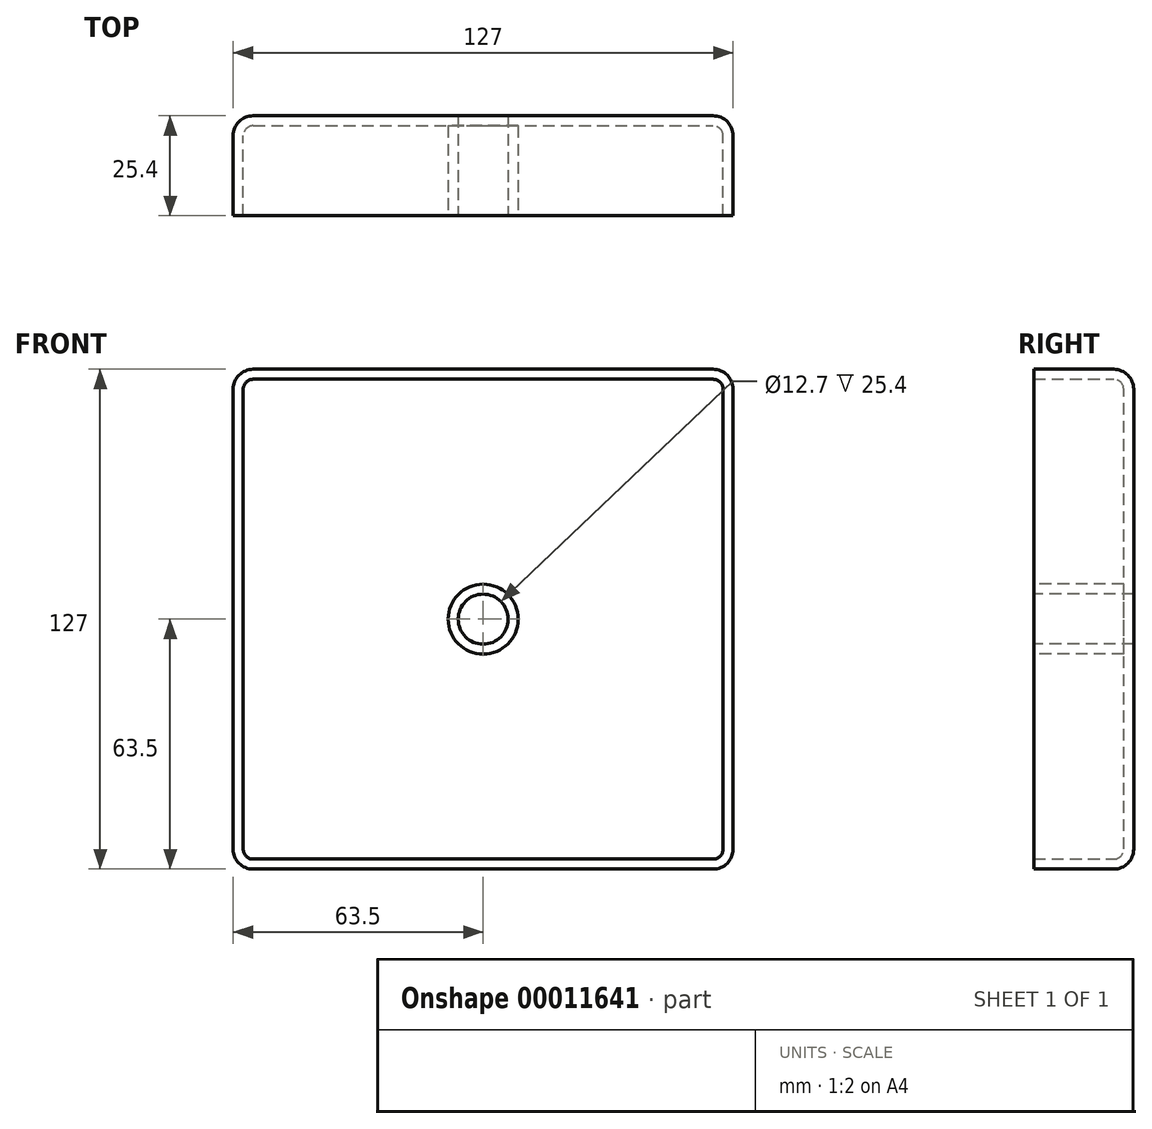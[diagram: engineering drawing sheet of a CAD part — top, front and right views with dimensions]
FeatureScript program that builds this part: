
annotation { "Feature Type Name" : "Feature", "Feature Type Description" : "" }
export const myFeature = defineFeature(function(context is Context, id is Id, definition is map)
    precondition{}
    {
        {
            var Q0;
            Q0=qCreatedBy(makeId("Front.planeOp"),FACE);
            var sketch = newSketch(context, id + "F0", { "sketchPlane" : qUnion([Q0])});
            skLineSegment(sketch, "E0.bottom", {"start": v(0, 0) * mm, "end": v(127, 0) * mm});
            skLineSegment(sketch, "E0.top", {"start": v(0, 127) * mm, "end": v(127, 127) * mm});
            skLineSegment(sketch, "E0.left", {"start": v(0, 0) * mm, "end": v(0, 127) * mm});
            skLineSegment(sketch, "E0.right", {"start": v(127, 0) * mm, "end": v(127, 127) * mm});
            skSolve(sketch);
        }
        {
            var Q0;
            Q0 = qSketchRegion(id + "F0", true);
            extrude(context, id + "F1", {"entities" : qUnion([Q0]), "depth" : 25.4 * mm});
        }
        {
            var Q0;
            Q0=makeQuery(id+"F1.opExtrude","CAP_FACE",FACE,{"disambiguationData":[OSD([sQuery(id+"F0.wireOp",EDGE,"E0.bottom"),sQuery(id+"F0.wireOp",EDGE,"E0.top"),sQuery(id+"F0.wireOp",EDGE,"E0.left"),sQuery(id+"F0.wireOp",EDGE,"E0.right")])],"isStart":false});
            var sketch = newSketch(context, id + "F2", { "sketchPlane" : qUnion([Q0])});
            skLineSegment(sketch, "E1", {"start": v(63.5, 127) * mm, "end": v(63.5, 0) * mm, "construction": true});
            skPoint(sketch, "E2", {"position": v(63.5, 63.5) * mm});
            skCircle(sketch, "E3", {"center": v(63.5, 63.5) * mm, "radius": 6.35 * mm});
            skSolve(sketch);
        }
        {
            var Q0;
            Q0=makeQuery(id+"F2.imprint","IMPRINT",FACE,{"disambiguationData":[TD([[makeQuery(id+"F2.imprint","IMPRINT",EDGE,{"derivedFrom":sQuery(id+"F2.wireOp",EDGE,"E3")}),1.0]])]});
            var Q1;
            Q1=sQuery(id+"F2.wireOp",EDGE,"E3");
            extrude(context, id + "F3", {"entities" : qUnion([Q0]), "operationType" : NewBodyOperationType.REMOVE, "surfaceEntities" : qUnion([Q1]), "endBound" : BoundingType.THROUGH_ALL, "oppositeDirection" : true, "depth" : 25.4 * mm});
        }
        {
            var Q0;
            Q0=makeQuery(id+"F1.opExtrude","CAP_EDGE",EDGE,{"disambiguationData":[OSD([sQuery(id+"F0.wireOp",EDGE,"E0.top")])],"isStart":true});
            var Q1;
            Q1=makeQuery(id+"F1.opExtrude","CAP_EDGE",EDGE,{"disambiguationData":[OSD([sQuery(id+"F0.wireOp",EDGE,"E0.left")])],"isStart":true});
            var Q2;
            Q2=makeQuery(id+"F1.opExtrude","CAP_EDGE",EDGE,{"disambiguationData":[OSD([sQuery(id+"F0.wireOp",EDGE,"E0.bottom")])],"isStart":true});
            var Q3;
            Q3=makeQuery(id+"F1.opExtrude","CAP_EDGE",EDGE,{"disambiguationData":[OSD([sQuery(id+"F0.wireOp",EDGE,"E0.right")])],"isStart":true});
            var Q4;
            Q4=makeQuery(id+"F1.opExtrude","SWEPT_EDGE",EDGE,{"disambiguationData":[OSD([sQuery(id+"F0.wireOp",EDGE,"E0.top"),sQuery(id+"F0.wireOp",EDGE,"E0.right")])]});
            var Q5;
            Q5=makeQuery(id+"F1.opExtrude","SWEPT_EDGE",EDGE,{"disambiguationData":[OSD([sQuery(id+"F0.wireOp",EDGE,"E0.top"),sQuery(id+"F0.wireOp",EDGE,"E0.left")])]});
            var Q6;
            Q6=makeQuery(id+"F1.opExtrude","SWEPT_EDGE",EDGE,{"disambiguationData":[OSD([sQuery(id+"F0.wireOp",EDGE,"E0.bottom"),sQuery(id+"F0.wireOp",EDGE,"E0.left")])]});
            var Q7;
            Q7=makeQuery(id+"F1.opExtrude","SWEPT_EDGE",EDGE,{"disambiguationData":[OSD([sQuery(id+"F0.wireOp",EDGE,"E0.bottom"),sQuery(id+"F0.wireOp",EDGE,"E0.right")])]});
            fillet(context, id + "F4", {"entities" : qUnion([Q0, Q1, Q2, Q3, Q4, Q5, Q6, Q7]), "radius" : 5.08 * mm, "tangentPropagation" : true, "allowEdgeOverflow" : false});
        }
        {
            var Q0;
            Q0=makeQuery(id+"F1.opExtrude","CAP_FACE",FACE,{"disambiguationData":[OSD([sQuery(id+"F0.wireOp",EDGE,"E0.bottom"),sQuery(id+"F0.wireOp",EDGE,"E0.top"),sQuery(id+"F0.wireOp",EDGE,"E0.left"),sQuery(id+"F0.wireOp",EDGE,"E0.right")])],"isStart":false});
            shell(context, id + "F5", {"entities" : qUnion([Q0]), "thickness" : 2.54 * mm});
        }
        {
            var Q0;
            Q0 = qSketchRegion(id + "F2", true);
            extrude(context, id + "F6", {"entities" : qUnion([Q0]), "operationType" : NewBodyOperationType.REMOVE, "endBound" : BoundingType.THROUGH_ALL, "oppositeDirection" : true, "depth" : 25.4 * mm});
        }
    });
